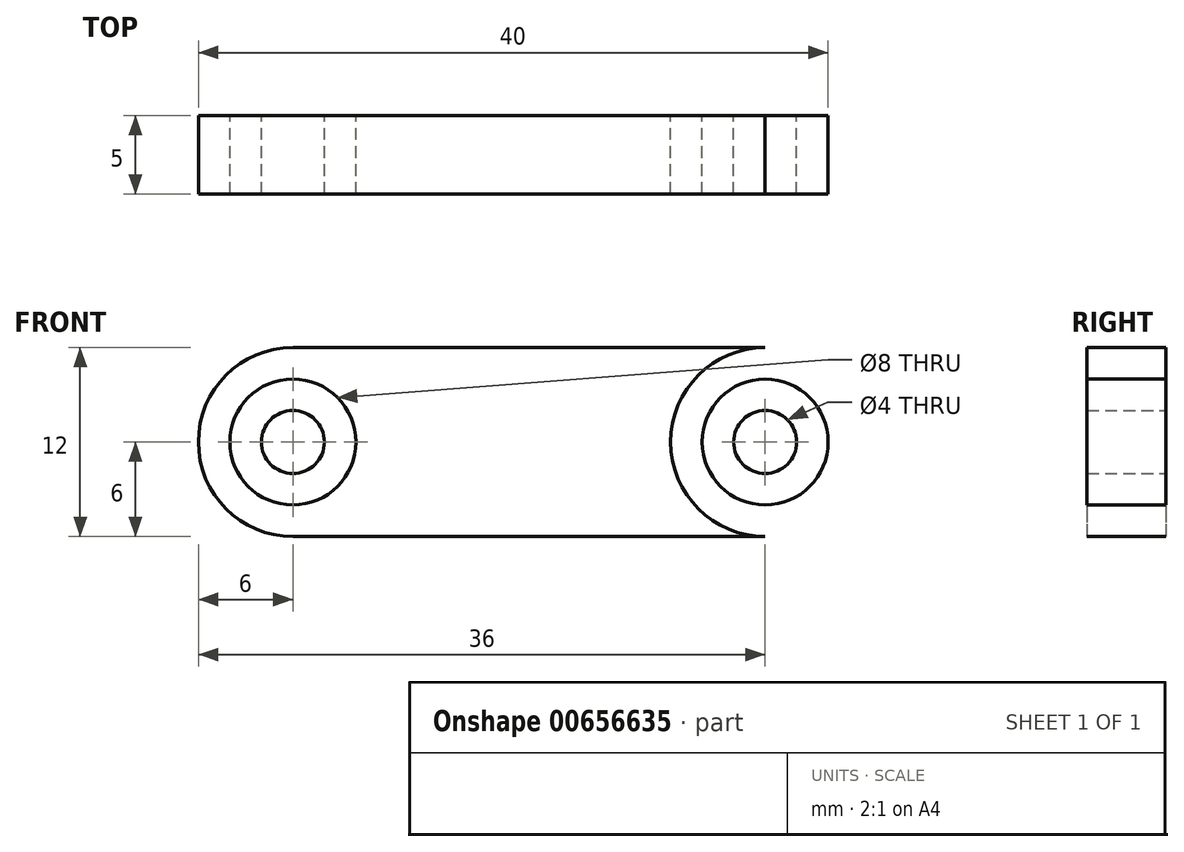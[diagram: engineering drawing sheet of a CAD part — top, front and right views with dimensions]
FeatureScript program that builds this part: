
annotation { "Feature Type Name" : "Feature", "Feature Type Description" : "" }
export const myFeature = defineFeature(function(context is Context, id is Id, definition is map)
    precondition{}
    {
        {
            var Q0;
            Q0=qCreatedBy(makeId("Front.planeOp"),FACE);
            var sketch = newSketch(context, id + "F0", { "sketchPlane" : qUnion([Q0])});
            skCircle(sketch, "E0", {"center": v(-15, 0) * mm, "radius": 6 * mm});
            skCircle(sketch, "E1", {"center": v(-15, 0) * mm, "radius": 4 * mm});
            skCircle(sketch, "E2", {"center": v(-15, 0) * mm, "radius": 2 * mm});
            skLineSegment(sketch, "E3", {"start": v(-15, 6) * mm, "end": v(0, 6) * mm});
            skLineSegment(sketch, "E4", {"start": v(-15, -6) * mm, "end": v(0, -6) * mm});
            skLineSegment(sketch, "E5.MirrorCS", {"start": v(15, -6) * mm, "end": v(0, -6) * mm});
            skLineSegment(sketch, "E6.MirrorCS", {"start": v(15, 6) * mm, "end": v(0, 6) * mm});
            skCircle(sketch, "E7.MirrorC", {"center": v(15, 0) * mm, "radius": 6 * mm});
            skCircle(sketch, "E8.MirrorC", {"center": v(15, 0) * mm, "radius": 2 * mm});
            skCircle(sketch, "E9.MirrorC", {"center": v(15, 0) * mm, "radius": 4 * mm});
            skSolve(sketch);
        }
        {
            var Q0;
            {var subQ1=sQuery(id+"F0.wireOp",EDGE,"E3");Q0=makeQuery(id+"F0.imprint","IMPRINT",FACE,{"disambiguationData":[TD([[makeQuery(id+"F0.imprint","IMPRINT",EDGE,{"derivedFrom":subQ1}),-1.0]])]});}
            var Q1;
            Q1=makeQuery(id+"F0.imprint","IMPRINT",FACE,{"disambiguationData":[TD([[makeQuery(id+"F0.imprint","IMPRINT",EDGE,{"derivedFrom":sQuery(id+"F0.wireOp",EDGE,"E1")}),-1.0]])]});
            var Q2;
            Q2=makeQuery(id+"F0.imprint","IMPRINT",FACE,{"disambiguationData":[TD([[makeQuery(id+"F0.imprint","IMPRINT",EDGE,{"derivedFrom":sQuery(id+"F0.wireOp",EDGE,"E2")}),1.0]])]});
            var Q3;
            Q3=makeQuery(id+"F0.imprint","IMPRINT",FACE,{"disambiguationData":[TD([[makeQuery(id+"F0.imprint","IMPRINT",EDGE,{"derivedFrom":sQuery(id+"F0.wireOp",EDGE,"E8.MirrorC")}),-1.0]])]});
            var Q4;
            Q4=makeQuery(id+"F0.imprint","IMPRINT",FACE,{"disambiguationData":[TD([[makeQuery(id+"F0.imprint","IMPRINT",EDGE,{"derivedFrom":sQuery(id+"F0.wireOp",EDGE,"E9.MirrorC")}),1.0]])]});
            extrude(context, id + "F1", {"entities" : qUnion([Q0, Q1, Q2, Q3, Q4]), "depth" : 5 * mm, "offsetDistance" : 25 * mm});
        }
    });
